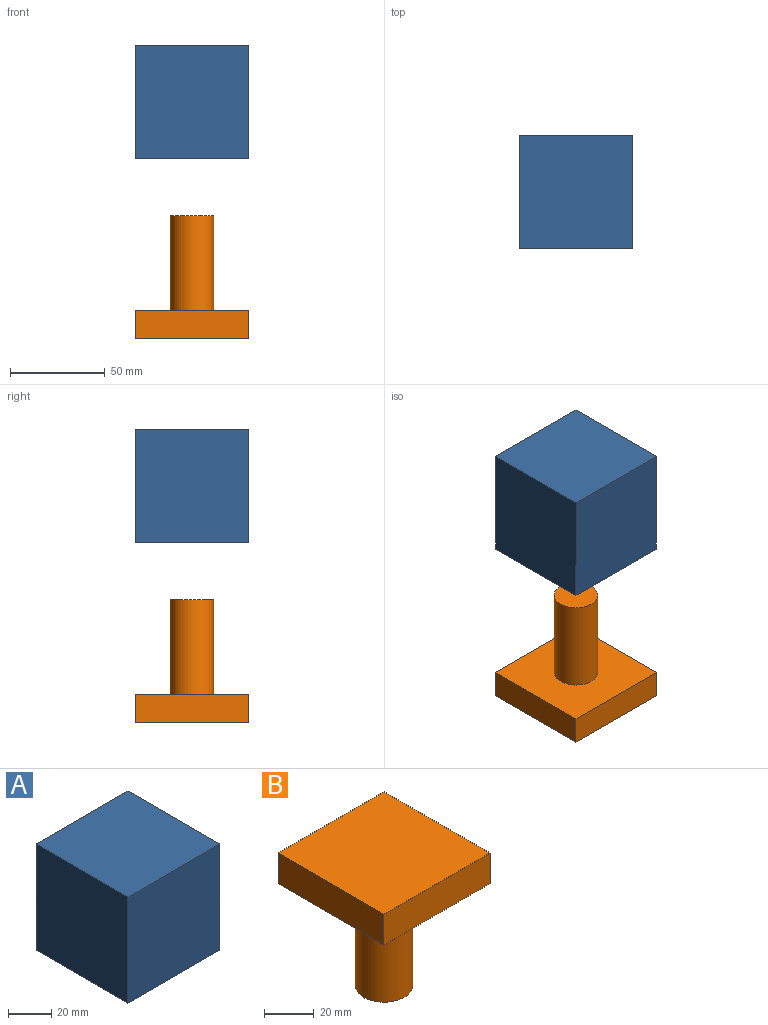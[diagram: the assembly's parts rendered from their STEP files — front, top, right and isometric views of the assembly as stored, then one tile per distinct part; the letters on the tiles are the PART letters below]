
ASSEMBLY  parts=2 mates=1
PART A: 8 faces, bbox 60x60x60 mm
  f0: plane 60x60mm, normal (0,0,-1), area 3109.1mm2, adj f1,f2,f3,f4,f6
  f1: plane 60x60mm, normal (0,1,0), area 3600mm2, adj f0,f2,f4,f5
  f2: plane 60x60mm, normal (-1,0,0), area 3600mm2, adj f0,f1,f3,f5
  f3: plane 60x60mm, normal (0,-1,0), area 3600mm2, adj f0,f2,f4,f5
  f4: plane 60x60mm, normal (1,0,0), area 3600mm2, adj f0,f1,f3,f5
  f5: plane 60x60mm, normal (0,0,1), area 3600mm2, adj f1,f2,f3,f4
  f6: cylinder r=12.5mm len=50mm, axis (0,0,-1), area 3927mm2, adj f0,f7
  f7: plane 25x25mm, normal (0,0,-1), area 490.9mm2, adj f6
PART B: 8 faces, bbox 60x60x65 mm
  f0: cylinder r=11.5mm len=50mm, axis (0,0,-1), area 3612.8mm2, adj f1,f7
  f1: plane 23x23mm, normal (0,0,-1), area 415.5mm2, adj f0
  f2: plane 60x15mm, normal (0,1,0), area 900mm2, adj f3,f5,f6,f7
  f3: plane 60x15mm, normal (-1,0,0), area 900mm2, adj f2,f4,f6,f7
  f4: plane 60x15mm, normal (0,-1,0), area 900mm2, adj f3,f5,f6,f7
  f5: plane 60x15mm, normal (1,0,0), area 900mm2, adj f2,f4,f6,f7
  f6: plane 60x60mm, normal (0,0,1), area 3600mm2, adj f2,f3,f4,f5
  f7: plane 60x60mm, normal (0,0,-1), area 3184.5mm2, adj f0,f2,f3,f4,f5
PLACE A t=(176.26,415.17,-23.96)mm
PLACE B rot(axis=(1,0,0),180deg) t=(-111.8,140.68,-53.96)mm
MATE slider B.f0 <-> A.f6  axis (0,0,1) through (-111.8,140.68,-53.96)mm
